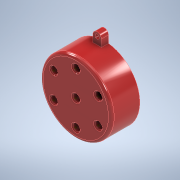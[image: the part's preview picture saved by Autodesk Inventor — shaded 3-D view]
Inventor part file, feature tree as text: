
AUTODESK INVENTOR PART (.ipt)
format: ipt  version: 2021 (Build 250183000, 183)  size: 192,000 bytes
history: native  units: mm
features: sketch x10, extrude x3, other x1, fillet x1, chamfer x1, pattern_circular x1, mirror x1
ambient origin geometry x8: Origin, YZ Plane, XZ Plane, XY Plane, X Axis, Y Axis, Z Axis, Center Point
bodies: Body1 (feature_tree)
feature tree (18):
  other  "Sólido1"
  extrude  "Extrusão1"  Depth=20.0mm TaperAngle=0.0deg
  fillet  "Arredondamento1"  Radius=2.0mm
  extrude  "Extrusão2"  Depth=5.0mm
  chamfer  "Chanfro1"  Distance=15.0mm
  pattern_circular  "Padrão circular1"  Count=6 Angle=360.0deg
  extrude  "Extrusão3"  Depth=3.0mm
  mirror  "Espelhamento1"
  sketch  "Esboço4"  dims[d9=0.6mm d10=2.0mm d11=45.0deg d12=60.0mm d13=360.0deg]
  sketch  "Esboço5"  dims[d15=6.0mm d16=3.0mm]
  sketch  "Esboço6"  dims[d17=30.0mm]
  sketch  "Esboço7"  dims[d18=5.0mm d19=0.0mm]
  sketch  "Esboço8"
  sketch  "Esboço9"
  sketch  "Esboço10"
  sketch  "Esboço1"  dims[d0=50.0mm d1=20.0mm d2=0.0mm d3=2.0mm]
  sketch  "Esboço2"  dims[d4=5.0mm d5=5.0mm]
  sketch  "Esboço3"  dims[d6=18.0mm d7=15.0mm d8=0.0mm]
